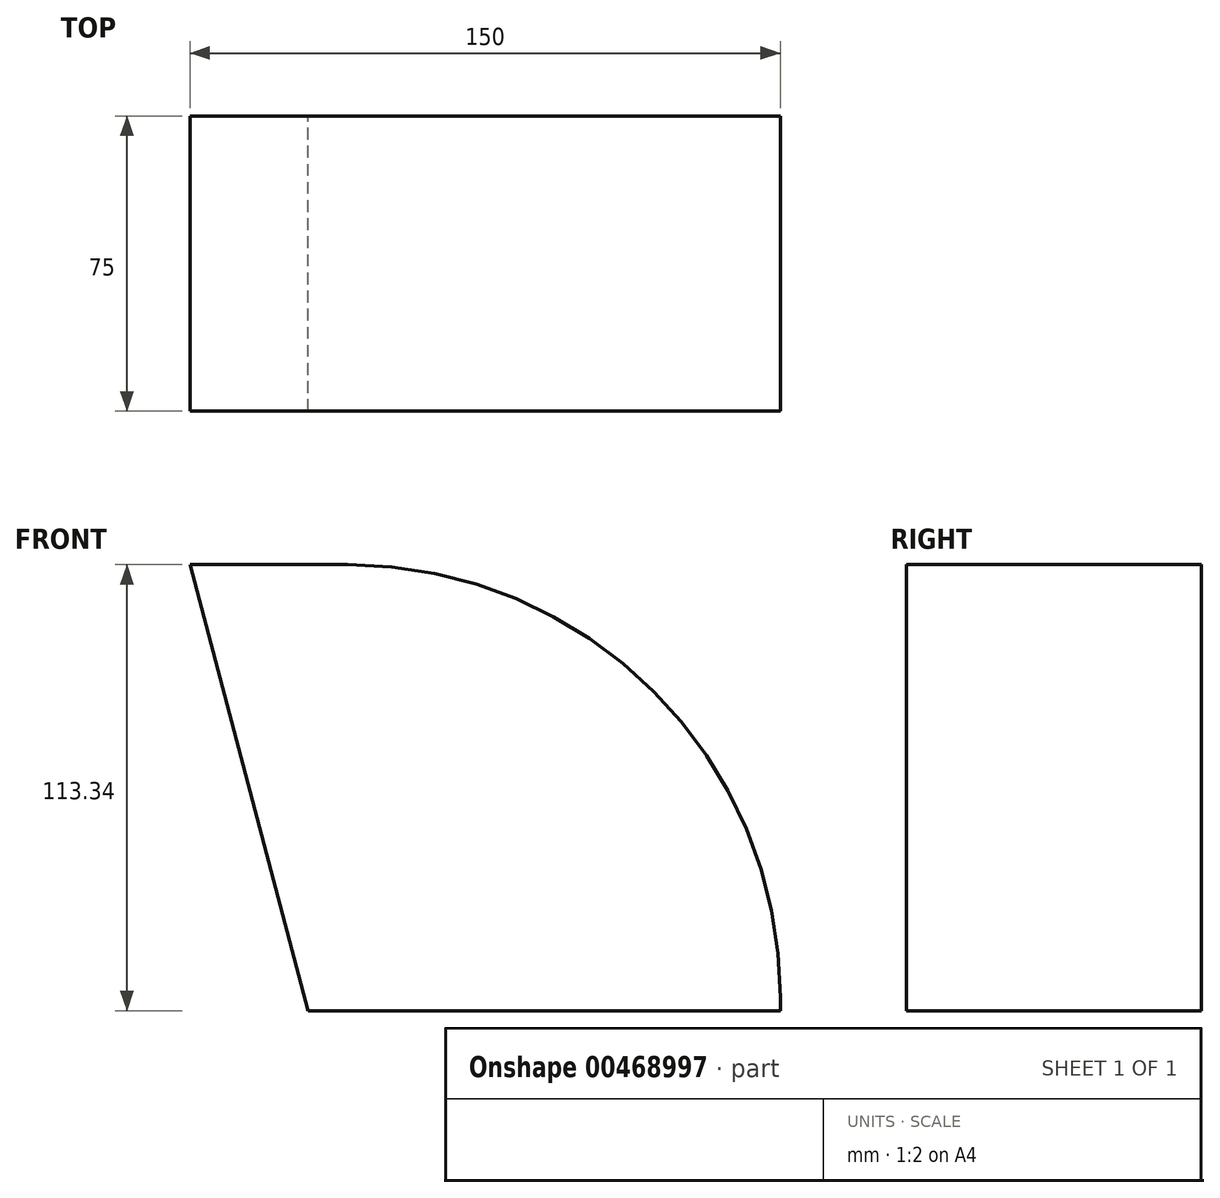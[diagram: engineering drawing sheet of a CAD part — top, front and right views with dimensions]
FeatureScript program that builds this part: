
annotation { "Feature Type Name" : "Feature", "Feature Type Description" : "" }
export const myFeature = defineFeature(function(context is Context, id is Id, definition is map)
    precondition{}
    {
        {
            var Q0;
            Q0=qCreatedBy(makeId("Front.planeOp"),FACE);
            var sketch = newSketch(context, id + "F0", { "sketchPlane" : qUnion([Q0])});
            skLineSegment(sketch, "E0.bottom", {"start": v(51.5, 0) * mm, "end": v(171.5, 0) * mm});
            skLineSegment(sketch, "E0.top", {"start": v(21.5, 113.34) * mm, "end": v(171.5, 113.34) * mm});
            skLineSegment(sketch, "E0.right", {"start": v(171.5, 0) * mm, "end": v(171.5, 113.34) * mm});
            skLineSegment(sketch, "E1", {"start": v(21.5, 113.34) * mm, "end": v(51.5, 0) * mm});
            skSolve(sketch);
        }
        {
            var Q0;
            Q0=makeQuery(id+"F0.imprint","IMPRINT",FACE,{"disambiguationData":[TD([[makeQuery(id+"F0.imprint","IMPRINT",EDGE,{"derivedFrom":sQuery(id+"F0.wireOp",EDGE,"E0.bottom")}),1.0]])]});
            extrude(context, id + "F1", {"entities" : qUnion([Q0]), "depth" : 75 * mm});
        }
        {
            var Q0;
            Q0=makeQuery(id+"F1.opExtrude","SWEPT_EDGE",EDGE,{"disambiguationData":[OSD([sQuery(id+"F0.wireOp",EDGE,"E0.top"),sQuery(id+"F0.wireOp",EDGE,"E0.right")])]});
            fillet(context, id + "F2", {"entities" : qUnion([Q0]), "radius" : 110 * mm, "tangentPropagation" : true, "allowEdgeOverflow" : false});
        }
    });
